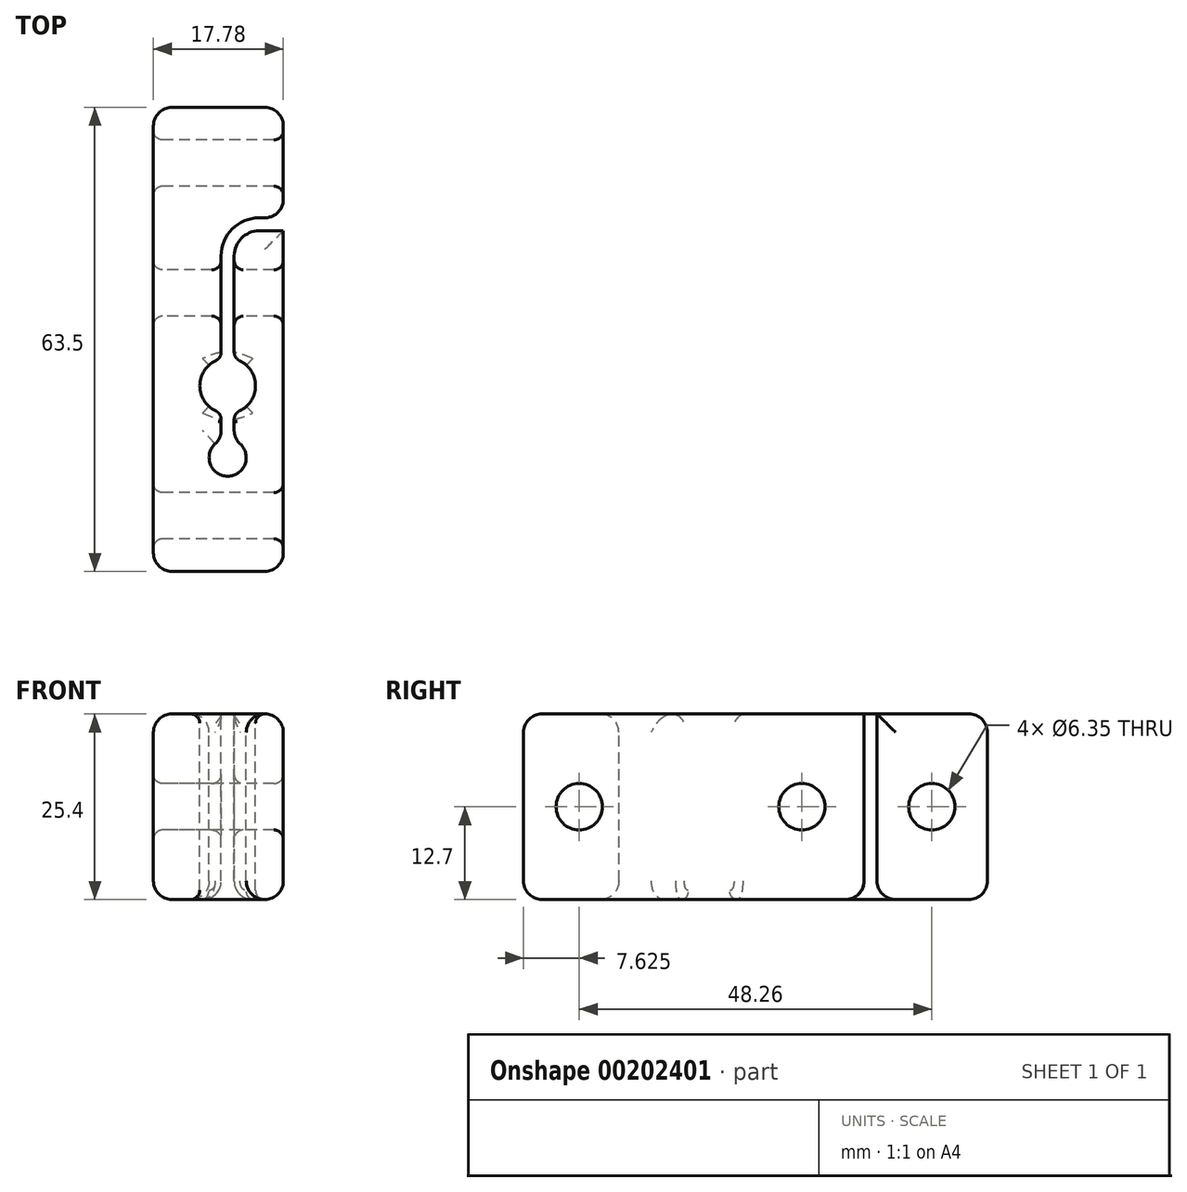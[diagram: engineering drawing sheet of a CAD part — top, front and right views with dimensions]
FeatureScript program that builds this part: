
annotation { "Feature Type Name" : "Feature", "Feature Type Description" : "" }
export const myFeature = defineFeature(function(context is Context, id is Id, definition is map)
    precondition{}
    {
        {
            var Q0;
            Q0=qCreatedBy(makeId("Top.planeOp"),FACE);
            var sketch = newSketch(context, id + "F0", { "sketchPlane" : qUnion([Q0])});
            skLineSegment(sketch, "E0", {"start": v(-46.47, 46.77) * mm, "end": v(-46.47, -16.73) * mm});
            skLineSegment(sketch, "E1", {"start": v(-46.47, -16.73) * mm, "end": v(-28.69, -16.73) * mm});
            skLineSegment(sketch, "E2", {"start": v(-28.69, -16.73) * mm, "end": v(-28.69, 46.77) * mm});
            skLineSegment(sketch, "E3", {"start": v(-28.69, 46.77) * mm, "end": v(-46.47, 46.77) * mm});
            skSolve(sketch);
        }
        {
            var Q0;
            Q0=makeQuery(id+"F0.imprint","IMPRINT",FACE,{"disambiguationData":[TD([[makeQuery(id+"F0.imprint","IMPRINT",EDGE,{"derivedFrom":sQuery(id+"F0.wireOp",EDGE,"E0")}),1.0]])]});
            extrude(context, id + "F1", {"entities" : qUnion([Q0]), "depth" : 25.4 * mm});
        }
        {
            var Q0;
            Q0=makeQuery(id+"F1.opExtrude","SWEPT_FACE",FACE,{"disambiguationData":[OSD([sQuery(id+"F0.wireOp",EDGE,"E0")])]});
            var sketch = newSketch(context, id + "F2", { "sketchPlane" : qUnion([Q0])});
            skCircle(sketch, "E4", {"center": v(-39.15, 12.7) * mm, "radius": 3.18 * mm});
            skCircle(sketch, "E5", {"center": v(9.1, 12.7) * mm, "radius": 3.18 * mm});
            skCircle(sketch, "E6", {"center": v(-21.37, 12.7) * mm, "radius": 3.18 * mm});
            skSolve(sketch);
        }
        {
            var Q0;
            Q0=makeQuery(id+"F2.imprint","IMPRINT",FACE,{"disambiguationData":[TD([[makeQuery(id+"F2.imprint","IMPRINT",EDGE,{"derivedFrom":sQuery(id+"F2.wireOp",EDGE,"E4")}),1.0]])]});
            var Q1;
            Q1=makeQuery(id+"F2.imprint","IMPRINT",FACE,{"disambiguationData":[TD([[makeQuery(id+"F2.imprint","IMPRINT",EDGE,{"derivedFrom":sQuery(id+"F2.wireOp",EDGE,"E6")}),1.0]])]});
            var Q2;
            Q2=makeQuery(id+"F2.imprint","IMPRINT",FACE,{"disambiguationData":[TD([[makeQuery(id+"F2.imprint","IMPRINT",EDGE,{"derivedFrom":sQuery(id+"F2.wireOp",EDGE,"E5")}),1.0]])]});
            extrude(context, id + "F3", {"entities" : qUnion([Q0, Q1, Q2]), "operationType" : NewBodyOperationType.REMOVE, "endBound" : BoundingType.THROUGH_ALL, "oppositeDirection" : true, "depth" : 25.4 * mm});
        }
        {
            var Q0;
            Q0=makeQuery(id+"F1.opExtrude","CAP_FACE",FACE,{"disambiguationData":[OSD([sQuery(id+"F0.wireOp",EDGE,"E0"),sQuery(id+"F0.wireOp",EDGE,"E1"),sQuery(id+"F0.wireOp",EDGE,"E2"),sQuery(id+"F0.wireOp",EDGE,"E3")])],"isStart":false});
            var sketch = newSketch(context, id + "F4", { "sketchPlane" : qUnion([Q0])});
            skCircle(sketch, "E7", {"center": v(-36.3, 8.67) * mm, "radius": 3.81 * mm});
            skLineSegment(sketch, "E8", {"start": v(-28.69, 29.88) * mm, "end": v(-32, 29.88) * mm});
            skArc(sketch, "E9", {"start": v(-32, 29.88) * mm, "mid": v(-34.42, 28.88) * mm, "end": v(-35.42, 26.46) * mm});
            skLineSegment(sketch, "E10", {"start": v(-35.42, 26.46) * mm, "end": v(-35.42, 12.38) * mm});
            skLineSegment(sketch, "E11.0", {"start": v(-37.2, 26.46) * mm, "end": v(-37.2, 12.38) * mm});
            skArc(sketch, "E11.1", {"start": v(-32, 31.66) * mm, "mid": v(-35.67, 30.14) * mm, "end": v(-37.2, 26.46) * mm});
            skLineSegment(sketch, "E11.2", {"start": v(-28.69, 31.66) * mm, "end": v(-32, 31.66) * mm});
            skLineSegment(sketch, "E12", {"start": v(-37.2, 4.97) * mm, "end": v(-37.2, 1.22) * mm});
            skLineSegment(sketch, "E13", {"start": v(-35.42, 4.97) * mm, "end": v(-35.42, 1.22) * mm});
            skCircle(sketch, "E14", {"center": v(-36.3, -1.16) * mm, "radius": 2.54 * mm});
            skSolve(sketch);
        }
        {
            var Q0;
            {var subQ4=sQuery(id+"F4.wireOp",EDGE,"E8");Q0=makeQuery(id+"F4.imprint","IMPRINT",FACE,{"disambiguationData":[TD([[makeQuery(id+"F4.imprint","IMPRINT",EDGE,{"derivedFrom":subQ4}),-1.0]])]});}
            var Q1;
            {var subQ0=sQuery(id+"F4.wireOp",EDGE,"E7");var subQ2=makeQuery(id+"F4.imprint","INTERSECT",VERTEX,{"derivedFrom":[subQ0,sQuery(id+"F4.wireOp",EDGE,"E10")]});Q1=makeQuery(id+"F4.imprint","IMPRINT",FACE,{"disambiguationData":[TD([[makeQuery(id+"F4.imprint","IMPRINT",EDGE,{"disambiguationData":[TD([[subQ2,-1.0]])],"derivedFrom":subQ0}),1.0]])]});}
            var Q2;
            {var subQ1=sQuery(id+"F4.wireOp",EDGE,"E12");Q2=makeQuery(id+"F4.imprint","IMPRINT",FACE,{"disambiguationData":[TD([[makeQuery(id+"F4.imprint","IMPRINT",EDGE,{"derivedFrom":subQ1}),1.0]])]});}
            var Q3;
            {var subQ0=sQuery(id+"F4.wireOp",EDGE,"E14");var subQ2=makeQuery(id+"F4.imprint","INTERSECT",VERTEX,{"derivedFrom":[sQuery(id+"F4.wireOp",EDGE,"E12"),subQ0]});Q3=makeQuery(id+"F4.imprint","IMPRINT",FACE,{"disambiguationData":[TD([[makeQuery(id+"F4.imprint","IMPRINT",EDGE,{"disambiguationData":[TD([[subQ2,1.0]])],"derivedFrom":subQ0}),1.0]])]});}
            extrude(context, id + "F5", {"entities" : qUnion([Q0, Q1, Q2, Q3]), "operationType" : NewBodyOperationType.REMOVE, "endBound" : BoundingType.THROUGH_ALL, "oppositeDirection" : true, "depth" : 25.4 * mm});
        }
        {
            var Q0;
            Q0=makeQuery(id+"F1.opExtrude","SWEPT_FACE",FACE,{"disambiguationData":[OSD([sQuery(id+"F0.wireOp",EDGE,"E1")])]});
            var Q1;
            Q1=makeQuery(id+"F1.opExtrude","SWEPT_FACE",FACE,{"disambiguationData":[OSD([sQuery(id+"F0.wireOp",EDGE,"E3")])]});
            var Q2;
            {var subQ0=sQuery(id+"F0.wireOp",EDGE,"E2");var subQ1=sQuery(id+"F0.wireOp",EDGE,"E1");Q2=makeQuery(id+"F5.boolean.opBoolean","SPLIT",EDGE,{"disambiguationData":[TD([makeQuery(id+"F1.opExtrude","SWEPT_FACE",FACE,{"disambiguationData":[OSD([subQ1])]})])],"derivedFrom":makeQuery(id+"F1.opExtrude","CAP_EDGE",EDGE,{"disambiguationData":[OSD([subQ0])],"isStart":false})});}
            var Q3;
            {var subQ0=sQuery(id+"F0.wireOp",EDGE,"E2");var subQ1=sQuery(id+"F0.wireOp",EDGE,"E3");Q3=makeQuery(id+"F5.boolean.opBoolean","SPLIT",EDGE,{"disambiguationData":[TD([makeQuery(id+"F1.opExtrude","SWEPT_FACE",FACE,{"disambiguationData":[OSD([subQ1])]})])],"derivedFrom":makeQuery(id+"F1.opExtrude","CAP_EDGE",EDGE,{"disambiguationData":[OSD([subQ0])],"isStart":false})});}
            var Q4;
            Q4=makeQuery(id+"F5.boolean.opBoolean","COPY",EDGE,{"derivedFrom":makeQuery(id+"F5.opExtrude","CAP_EDGE",EDGE,{"disambiguationData":[OSD([sQuery(id+"F4.wireOp",EDGE,"E11.0")])],"isStart":true})});
            var Q5;
            Q5=makeQuery(id+"F5.boolean.opBoolean","COPY",EDGE,{"derivedFrom":makeQuery(id+"F5.opExtrude","CAP_EDGE",EDGE,{"disambiguationData":[OSD([sQuery(id+"F4.wireOp",EDGE,"E10")])],"isStart":true})});
            var Q6;
            Q6=makeQuery(id+"F5.boolean.opBoolean","COPY",EDGE,{"derivedFrom":makeQuery(id+"F5.opExtrude","SWEPT_EDGE",EDGE,{"disambiguationData":[OSD([sQuery(id+"F0.wireOp",EDGE,"E2"),sQuery(id+"F4.wireOp",EDGE,"E8")])]})});
            var Q7;
            Q7=makeQuery(id+"F5.boolean.opBoolean","COPY",EDGE,{"derivedFrom":makeQuery(id+"F5.opExtrude","SWEPT_EDGE",EDGE,{"disambiguationData":[OSD([sQuery(id+"F0.wireOp",EDGE,"E2"),sQuery(id+"F4.wireOp",EDGE,"E11.2")])]})});
            var Q8;
            Q8=makeQuery(id+"F5.boolean.opBoolean","INTERSECT",EDGE,{"derivedFrom":[makeQuery(id+"F1.opExtrude","CAP_FACE",FACE,{"disambiguationData":[OSD([sQuery(id+"F0.wireOp",EDGE,"E0"),sQuery(id+"F0.wireOp",EDGE,"E1"),sQuery(id+"F0.wireOp",EDGE,"E2"),sQuery(id+"F0.wireOp",EDGE,"E3")])],"isStart":true}),makeQuery(id+"F5.opExtrude","SWEPT_FACE",FACE,{"disambiguationData":[OSD([sQuery(id+"F4.wireOp",EDGE,"E11.0")])]})]});
            var Q9;
            Q9=makeQuery(id+"F5.boolean.opBoolean","INTERSECT",EDGE,{"derivedFrom":[makeQuery(id+"F1.opExtrude","CAP_FACE",FACE,{"disambiguationData":[OSD([sQuery(id+"F0.wireOp",EDGE,"E0"),sQuery(id+"F0.wireOp",EDGE,"E1"),sQuery(id+"F0.wireOp",EDGE,"E2"),sQuery(id+"F0.wireOp",EDGE,"E3")])],"isStart":true}),makeQuery(id+"F5.opExtrude","SWEPT_FACE",FACE,{"disambiguationData":[OSD([sQuery(id+"F4.wireOp",EDGE,"E10")])]})]});
            var Q10;
            {var subQ0=sQuery(id+"F0.wireOp",EDGE,"E2");var subQ1=sQuery(id+"F0.wireOp",EDGE,"E1");Q10=makeQuery(id+"F5.boolean.opBoolean","SPLIT",EDGE,{"disambiguationData":[TD([makeQuery(id+"F1.opExtrude","SWEPT_FACE",FACE,{"disambiguationData":[OSD([subQ1])]})])],"derivedFrom":makeQuery(id+"F1.opExtrude","CAP_EDGE",EDGE,{"disambiguationData":[OSD([subQ0])],"isStart":true})});}
            var Q11;
            {var subQ0=sQuery(id+"F0.wireOp",EDGE,"E2");var subQ1=sQuery(id+"F0.wireOp",EDGE,"E3");Q11=makeQuery(id+"F5.boolean.opBoolean","SPLIT",EDGE,{"disambiguationData":[TD([makeQuery(id+"F1.opExtrude","SWEPT_FACE",FACE,{"disambiguationData":[OSD([subQ1])]})])],"derivedFrom":makeQuery(id+"F1.opExtrude","CAP_EDGE",EDGE,{"disambiguationData":[OSD([subQ0])],"isStart":true})});}
            var Q12;
            Q12=makeQuery(id+"F1.opExtrude","CAP_EDGE",EDGE,{"disambiguationData":[OSD([sQuery(id+"F0.wireOp",EDGE,"E0")])],"isStart":false});
            var Q13;
            Q13=makeQuery(id+"F1.opExtrude","CAP_EDGE",EDGE,{"disambiguationData":[OSD([sQuery(id+"F0.wireOp",EDGE,"E0")])],"isStart":true});
            var Q14;
            Q14=makeQuery(id+"F5.boolean.opBoolean","COPY",EDGE,{"derivedFrom":makeQuery(id+"F5.opExtrude","CAP_EDGE",EDGE,{"disambiguationData":[OSD([sQuery(id+"F4.wireOp",EDGE,"E12")])],"isStart":true})});
            var Q15;
            Q15=makeQuery(id+"F5.boolean.opBoolean","COPY",EDGE,{"derivedFrom":makeQuery(id+"F5.opExtrude","CAP_EDGE",EDGE,{"disambiguationData":[OSD([sQuery(id+"F4.wireOp",EDGE,"E13")])],"isStart":true})});
            var Q16;
            Q16=makeQuery(id+"F5.boolean.opBoolean","COPY",FACE,{"derivedFrom":makeQuery(id+"F5.opExtrude","SWEPT_FACE",FACE,{"disambiguationData":[OSD([sQuery(id+"F4.wireOp",EDGE,"E14")])]})});
            var Q17;
            Q17=makeQuery(id+"F5.boolean.opBoolean","INTERSECT",EDGE,{"derivedFrom":[makeQuery(id+"F1.opExtrude","CAP_FACE",FACE,{"disambiguationData":[OSD([sQuery(id+"F0.wireOp",EDGE,"E0"),sQuery(id+"F0.wireOp",EDGE,"E1"),sQuery(id+"F0.wireOp",EDGE,"E2"),sQuery(id+"F0.wireOp",EDGE,"E3")])],"isStart":true}),makeQuery(id+"F5.opExtrude","SWEPT_FACE",FACE,{"disambiguationData":[OSD([sQuery(id+"F4.wireOp",EDGE,"E13")])]})]});
            var Q18;
            Q18=makeQuery(id+"F5.boolean.opBoolean","INTERSECT",EDGE,{"derivedFrom":[makeQuery(id+"F1.opExtrude","CAP_FACE",FACE,{"disambiguationData":[OSD([sQuery(id+"F0.wireOp",EDGE,"E0"),sQuery(id+"F0.wireOp",EDGE,"E1"),sQuery(id+"F0.wireOp",EDGE,"E2"),sQuery(id+"F0.wireOp",EDGE,"E3")])],"isStart":true}),makeQuery(id+"F5.opExtrude","SWEPT_FACE",FACE,{"disambiguationData":[OSD([sQuery(id+"F4.wireOp",EDGE,"E12")])]})]});
            fillet(context, id + "F6", {"entities" : qUnion([Q0, Q1, Q2, Q3, Q4, Q5, Q6, Q7, Q8, Q9, Q10, Q11, Q12, Q13, Q14, Q15, Q16, Q17, Q18]), "radius" : 2.54 * mm, "tangentPropagation" : true, "allowEdgeOverflow" : false});
        }
        {
            var Q0;
            Q0=makeQuery(id+"F5.boolean.opBoolean","COPY",FACE,{"derivedFrom":makeQuery(id+"F5.opExtrude","SWEPT_FACE",FACE,{"disambiguationData":[OSD([sQuery(id+"F4.wireOp",EDGE,"E7")])]})});
            var Q1;
            Q1=makeQuery(id+"F3.boolean.opBoolean","COPY",FACE,{"derivedFrom":makeQuery(id+"F3.opExtrude","SWEPT_FACE",FACE,{"disambiguationData":[OSD([sQuery(id+"F2.wireOp",EDGE,"E5")])]})});
            var Q2;
            Q2=makeQuery(id+"F5.boolean.opBoolean","SPLIT",FACE,{"disambiguationData":[TD([makeQuery(id+"F1.opExtrude","SWEPT_FACE",FACE,{"disambiguationData":[OSD([sQuery(id+"F0.wireOp",EDGE,"E2")])]})])],"derivedFrom":makeQuery(id+"F3.boolean.opBoolean","COPY",FACE,{"derivedFrom":makeQuery(id+"F3.opExtrude","SWEPT_FACE",FACE,{"disambiguationData":[OSD([sQuery(id+"F2.wireOp",EDGE,"E6")])]})})});
            var Q3;
            Q3=makeQuery(id+"F3.boolean.opBoolean","COPY",FACE,{"derivedFrom":makeQuery(id+"F3.opExtrude","SWEPT_FACE",FACE,{"disambiguationData":[OSD([sQuery(id+"F2.wireOp",EDGE,"E4")])]})});
            var Q4;
            Q4=makeQuery(id+"F5.boolean.opBoolean","SPLIT",FACE,{"disambiguationData":[TD([makeQuery(id+"F1.opExtrude","SWEPT_FACE",FACE,{"disambiguationData":[OSD([sQuery(id+"F0.wireOp",EDGE,"E0")])]})])],"derivedFrom":makeQuery(id+"F3.boolean.opBoolean","COPY",FACE,{"derivedFrom":makeQuery(id+"F3.opExtrude","SWEPT_FACE",FACE,{"disambiguationData":[OSD([sQuery(id+"F2.wireOp",EDGE,"E6")])]})})});
            fillet(context, id + "F7", {"entities" : qUnion([Q0, Q1, Q2, Q3, Q4]), "radius" : 1.27 * mm, "tangentPropagation" : true, "allowEdgeOverflow" : false});
        }
    });
